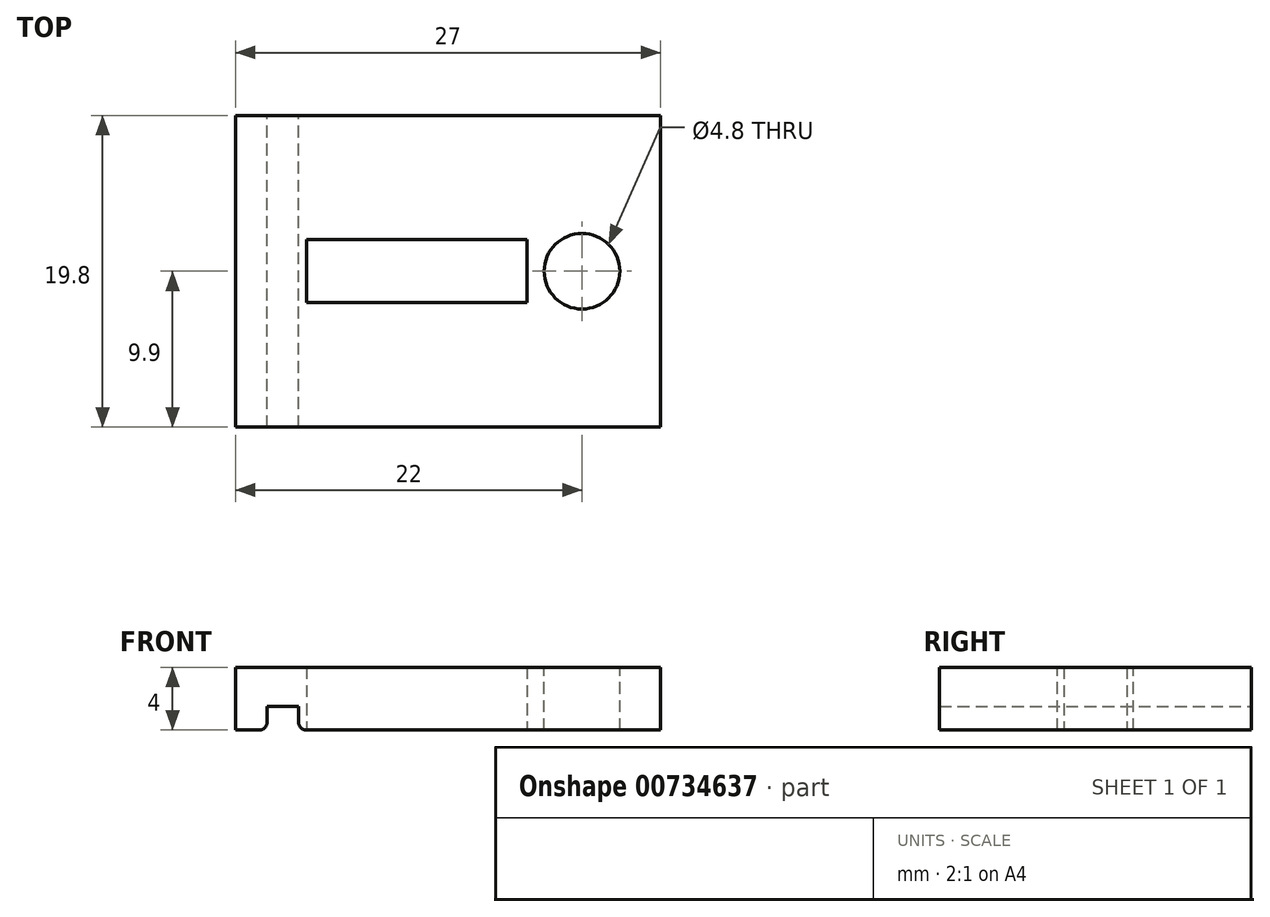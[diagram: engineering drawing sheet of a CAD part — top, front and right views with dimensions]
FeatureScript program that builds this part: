
annotation { "Feature Type Name" : "Feature", "Feature Type Description" : "" }
export const myFeature = defineFeature(function(context is Context, id is Id, definition is map)
    precondition{}
    {
        {
            var Q0;
            Q0=qCreatedBy(makeId("Front.planeOp"),FACE);
            var sketch = newSketch(context, id + "F0", { "sketchPlane" : qUnion([Q0])});
            skLineSegment(sketch, "E0.bottom", {"start": v(0, 0) * mm, "end": v(-23, 0) * mm});
            skLineSegment(sketch, "E0.top", {"start": v(0, 4) * mm, "end": v(-27, 4) * mm});
            skLineSegment(sketch, "E0.left", {"start": v(0, 0) * mm, "end": v(0, 4) * mm});
            skLineSegment(sketch, "E0.right", {"start": v(-27, 0) * mm, "end": v(-27, 4) * mm});
            skLineSegment(sketch, "E1.top", {"start": v(-25, 1.5) * mm, "end": v(-23, 1.5) * mm});
            skLineSegment(sketch, "E1.left", {"start": v(-25, 0) * mm, "end": v(-25, 1.5) * mm});
            skLineSegment(sketch, "E1.right", {"start": v(-23, 0) * mm, "end": v(-23, 1.5) * mm});
            skLineSegment(sketch, "E2.trimOffspring", {"start": v(-25, 0) * mm, "end": v(-27, 0) * mm});
            skSolve(sketch);
        }
        {
            var Q0;
            Q0 = qSketchRegion(id + "F0", true);
            extrude(context, id + "F1", {"entities" : qUnion([Q0]), "depth" : 9.9 * mm, "offsetDistance" : 25 * mm, "hasSecondDirection" : true, "secondDirectionOppositeDirection" : true, "secondDirectionDepth" : 9.9 * mm});
        }
        {
            var Q0;
            Q0=makeQuery(id+"F1.opExtrude","SWEPT_FACE",FACE,{"disambiguationData":[OSD([sQuery(id+"F0.wireOp",EDGE,"E0.top")])]});
            var sketch = newSketch(context, id + "F2", { "sketchPlane" : qUnion([Q0])});
            skCircle(sketch, "E3", {"center": v(-5, 0) * mm, "radius": 2.4 * mm});
            skSolve(sketch);
        }
        {
            var Q0;
            Q0 = qSketchRegion(id + "F2", true);
            extrude(context, id + "F3", {"entities" : qUnion([Q0]), "operationType" : NewBodyOperationType.REMOVE, "endBound" : BoundingType.THROUGH_ALL, "oppositeDirection" : true, "depth" : 25 * mm, "offsetDistance" : 25 * mm});
        }
        {
            var Q0;
            Q0=makeQuery(id+"F1.opExtrude","SWEPT_EDGE",EDGE,{"disambiguationData":[OSD([sQuery(id+"F0.wireOp",EDGE,"E1.left"),sQuery(id+"F0.wireOp",EDGE,"E2.trimOffspring")])]});
            var Q1;
            Q1=makeQuery(id+"F1.opExtrude","SWEPT_EDGE",EDGE,{"disambiguationData":[OSD([sQuery(id+"F0.wireOp",EDGE,"E0.bottom"),sQuery(id+"F0.wireOp",EDGE,"E1.right")])]});
            fillet(context, id + "F4", {"entities" : qUnion([Q0, Q1]), "tangentPropagation" : true, "radius" : 0.5 * mm, "defaultsChanged" : false, "vertexSettings" : [], "allowEdgeOverflow" : false});
        }
        {
            var Q0;
            Q0=makeQuery(id+"F1.opExtrude","SWEPT_FACE",FACE,{"disambiguationData":[OSD([sQuery(id+"F0.wireOp",EDGE,"E0.bottom")])]});
            var sketch = newSketch(context, id + "F5", { "sketchPlane" : qUnion([Q0])});
            skLineSegment(sketch, "E4.bottom", {"start": v(-22.5, 2) * mm, "end": v(-8.5, 2) * mm});
            skLineSegment(sketch, "E4.top", {"start": v(-22.5, -2) * mm, "end": v(-8.5, -2) * mm});
            skLineSegment(sketch, "E4.left", {"start": v(-22.5, 2) * mm, "end": v(-22.5, -2) * mm});
            skLineSegment(sketch, "E4.right", {"start": v(-8.5, 2) * mm, "end": v(-8.5, -2) * mm});
            skSolve(sketch);
        }
        {
            var Q0;
            Q0 = qSketchRegion(id + "F5", true);
            extrude(context, id + "F6", {"entities" : qUnion([Q0]), "operationType" : NewBodyOperationType.REMOVE, "endBound" : BoundingType.THROUGH_ALL, "oppositeDirection" : true, "depth" : 25 * mm, "offsetDistance" : 25 * mm});
        }
    });
